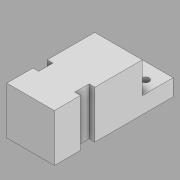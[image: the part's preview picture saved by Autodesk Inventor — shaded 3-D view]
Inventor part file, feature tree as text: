
AUTODESK INVENTOR PART (.ipt)
format: ipt  version: 2020 (Build 240168000, 168)  size: 136,192 bytes
history: native  units: in
note: dims shown in document units (in); Inventor stores cm internally (conversion verified against a paired STEP export)
features: sketch x4, extrude x3, other x1, hole x1
ambient origin geometry x8: Origin, YZ Plane, XZ Plane, XY Plane, X Axis, Y Axis, Z Axis, Center Point
bodies: Body1 (feature_tree)
feature tree (9):
  other  "Sólido1"
  extrude  "Extrusión1"  Depth=3.7in
  extrude  "Extrusión2"  Depth=0.6in
  extrude  "Extrusión4"  Depth=0.6in
  hole  "Agujero1"  [1 undecoded]
  sketch  "Boceto1"  dims[d0=2.0in d1=3.7in]
  sketch  "Boceto2"  dims[d2=1.1in d3=0.6in]
  sketch  "Boceto4"  dims[d4=0.24in d5=1.1in d6=0.6in]
  sketch  "Boceto5"  dims[d7=0.24in d8=2.0in d9=0.0in d10=2.0in d11=1.3in d12=0.7in d13=0.0in d19=1.5in d20=1.0in d21=1.0in d22=1.7in d23=0.0in d24=0.5in d25=0.5in d26=1.0in d27=0.66in d28=0.3in d29=0.25in d30=0.38in d31=0.3in d32=0.5635in d33=1.0in d34=0.8108in]
note: 1 required parameter value undecoded (feature->parameter linkage not recoverable at this tier; creation-order binding heuristic only, values carry confidence <= 0.55)
